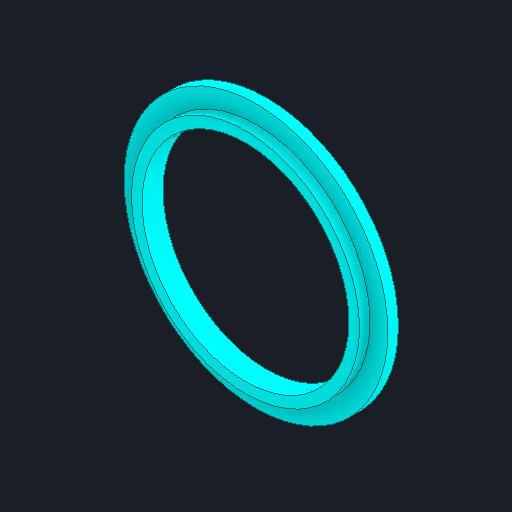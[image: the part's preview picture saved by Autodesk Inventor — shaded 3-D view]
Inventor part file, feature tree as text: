
AUTODESK INVENTOR PART (.ipt)
format: ipt  version: 2023.4 (Build 274418000, 418)  size: 211,968 bytes
history: native  units: mm
features: other x3, sketch x2, extrude x2, plane x1, reference x1
ambient origin geometry x8: Origin, YZ Plane, XZ Plane, XY Plane, X Axis, Y Axis, Z Axis, Center Point
bodies: Solid1 (feature_tree)
feature tree (9):
  sketch  "Sketch1"  dims[d0=0.0375mm d1=1.25mm]
  plane  "Work Plane1"
  extrude  "Extrusion1"  Depth=1.25mm
  extrude  "Extrusion2"  Depth=1.25mm
  reference  "Reference1"
  sketch  "Sketch2"  dims[d2=1.25mm d3=0.0mm d4=0.125mm d5=2.0mm d6=1.25mm d7=0.0mm]
  other  "<path>\Projects\Project Protocube\Protocube\CAD, STL, OBJ Files\1 CAD\Cube 1x1 V5.iam"
  other  "Cube 1x1 V5.iam"
  other  "One Inch Lense Holder (V5):1"
note: 1 file-system path scrubbed to <path> (originals preserved in map.json)
